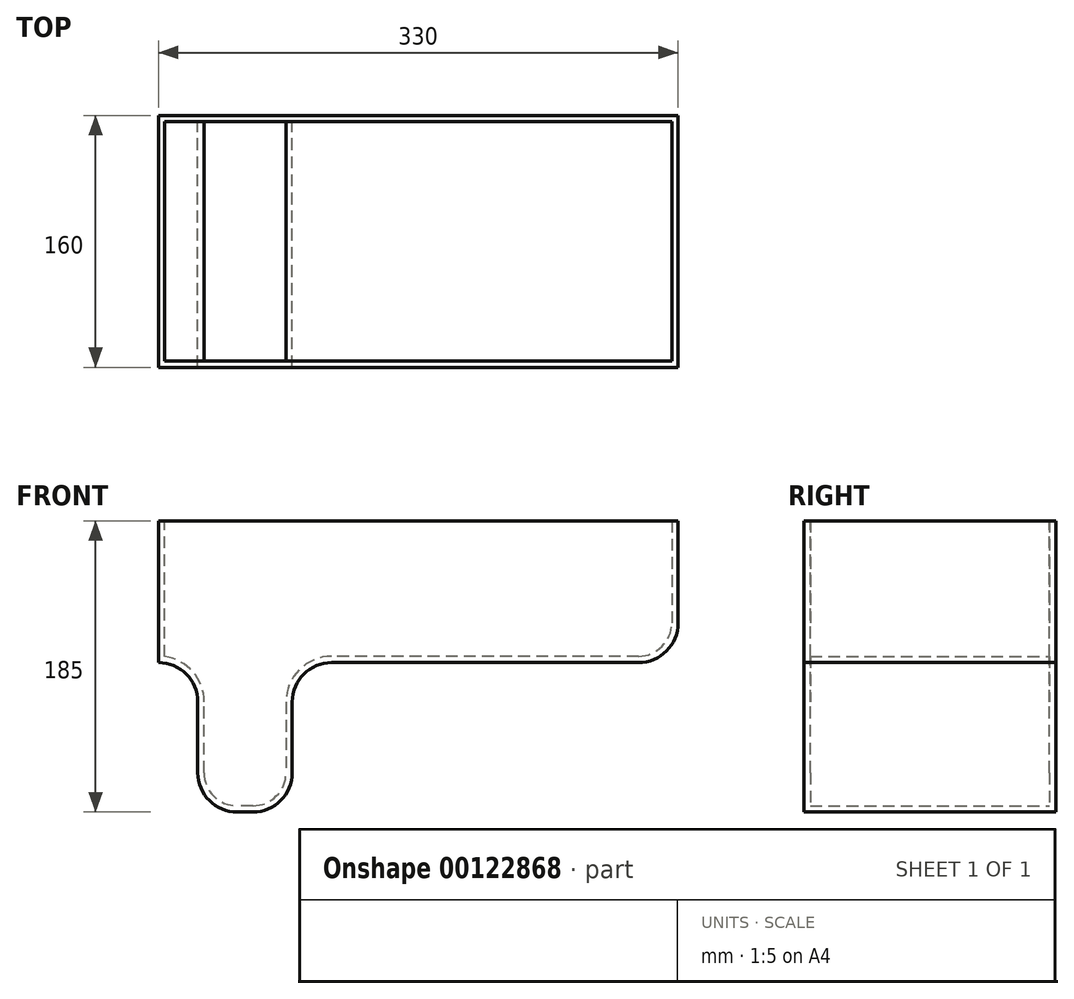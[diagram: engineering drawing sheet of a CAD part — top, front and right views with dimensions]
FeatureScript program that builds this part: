
annotation { "Feature Type Name" : "Feature", "Feature Type Description" : "" }
export const myFeature = defineFeature(function(context is Context, id is Id, definition is map)
    precondition{}
    {
        {
            var Q0;
            Q0=qCreatedBy(makeId("Front.planeOp"),FACE);
            var sketch = newSketch(context, id + "F0", { "sketchPlane" : qUnion([Q0])});
            skLineSegment(sketch, "E0", {"start": v(0, -25) * mm, "end": v(0, -70) * mm});
            skLineSegment(sketch, "E1", {"start": v(-25, -95) * mm, "end": v(-35, -95) * mm});
            skLineSegment(sketch, "E2", {"start": v(-60, -70) * mm, "end": v(-60, -25) * mm});
            skLineSegment(sketch, "E3", {"start": v(-85, 0) * mm, "end": v(-85, 0) * mm});
            skLineSegment(sketch, "E4", {"start": v(-85, 0) * mm, "end": v(-85, 90) * mm});
            skLineSegment(sketch, "E5", {"start": v(-85, 90) * mm, "end": v(245, 90) * mm});
            skLineSegment(sketch, "E6", {"start": v(245, 90) * mm, "end": v(245, 25) * mm});
            skLineSegment(sketch, "E7", {"start": v(220, 0) * mm, "end": v(25, 0) * mm});
            skPoint(sketch, "E8.visualSharp", {"position": v(245, 0) * mm});
            skArc(sketch, "E8.filletArc", {"start": v(220, 0) * mm, "mid": v(237.68, 7.32) * mm, "end": v(245, 25) * mm});
            skPoint(sketch, "E9.visualSharp", {"position": v(0, 0) * mm});
            skArc(sketch, "E9.filletArc", {"start": v(25, 0) * mm, "mid": v(7.32, -7.32) * mm, "end": v(0, -25) * mm});
            skPoint(sketch, "E10.visualSharp", {"position": v(0, -95) * mm});
            skArc(sketch, "E10.filletArc", {"start": v(-25, -95) * mm, "mid": v(-7.32, -87.68) * mm, "end": v(0, -70) * mm});
            skPoint(sketch, "E11.visualSharp", {"position": v(-60, -95) * mm});
            skArc(sketch, "E11.filletArc", {"start": v(-60, -70) * mm, "mid": v(-52.68, -87.68) * mm, "end": v(-35, -95) * mm});
            skPoint(sketch, "E12.visualSharp", {"position": v(-60, 0) * mm});
            skArc(sketch, "E12.filletArc", {"start": v(-60, -25) * mm, "mid": v(-67.32, -7.32) * mm, "end": v(-85, 0) * mm});
            skLineSegment(sketch, "E13", {"start": v(25, 0) * mm, "end": v(-85, 0) * mm});
            skSolve(sketch);
        }
        {
            var Q0;
            Q0=qSketchRegion(id+"F0",true);
            extrude(context, id + "F1", {"entities" : qUnion([Q0]), "depth" : 160 * mm});
        }
        {
            var Q0;
            Q0=qCreatedBy(makeId("Front.planeOp"),FACE);
            cPlane(context, id + "F2", {"entities" : qUnion([Q0]), "cplaneType" : CPlaneType.OFFSET, "offset" : 4 * mm, "width" : 150 * mm, "height" : 150 * mm});
        }
        {
            var Q0;
            Q0=qCreatedBy(id+"F2.planeOp",FACE);
            var sketch = newSketch(context, id + "F3", { "sketchPlane" : qUnion([Q0])});
            skArc(sketch, "E14.0", {"start": v(25, 0) * mm, "mid": v(7.32, -7.32) * mm, "end": v(0, -25) * mm});
            skLineSegment(sketch, "E15.0", {"start": v(0, -25) * mm, "end": v(0, -70) * mm});
            skArc(sketch, "E16.0", {"start": v(-25, -95) * mm, "mid": v(-7.32, -87.68) * mm, "end": v(0, -70) * mm});
            skLineSegment(sketch, "E17.0", {"start": v(-25, -95) * mm, "end": v(-35, -95) * mm});
            skArc(sketch, "E18.0", {"start": v(-60, -70) * mm, "mid": v(-52.68, -87.68) * mm, "end": v(-35, -95) * mm});
            skLineSegment(sketch, "E19.0", {"start": v(-60, -70) * mm, "end": v(-60, -25) * mm});
            skArc(sketch, "E20.0", {"start": v(-60, -25) * mm, "mid": v(-67.32, -7.32) * mm, "end": v(-85, 0) * mm});
            skLineSegment(sketch, "E21.6", {"start": v(-25, -91) * mm, "end": v(-35, -91) * mm});
            skLineSegment(sketch, "E22.1", {"start": v(-56, -70) * mm, "end": v(-56, -25) * mm});
            skArc(sketch, "E22.2", {"start": v(-56, -70) * mm, "mid": v(-49.85, -84.85) * mm, "end": v(-35, -91) * mm});
            skArc(sketch, "E22.3", {"start": v(25, 4) * mm, "mid": v(4.5, -4.5) * mm, "end": v(-4, -25) * mm});
            skLineSegment(sketch, "E22.4", {"start": v(-4, -25) * mm, "end": v(-4, -70) * mm});
            skArc(sketch, "E22.5", {"start": v(-25, -91) * mm, "mid": v(-10.15, -84.85) * mm, "end": v(-4, -70) * mm});
            skLineSegment(sketch, "E23.0", {"start": v(241, 90) * mm, "end": v(241, 25) * mm});
            skLineSegment(sketch, "E24.0", {"start": v(-81, 3.72) * mm, "end": v(-81, 90) * mm});
            skLineSegment(sketch, "E25.0", {"start": v(-85, 90) * mm, "end": v(245, 90) * mm});
            skLineSegment(sketch, "E26.0", {"start": v(220, 4) * mm, "end": v(25, 4) * mm});
            skArc(sketch, "E26.1", {"start": v(220, 4) * mm, "mid": v(234.85, 10.15) * mm, "end": v(241, 25) * mm});
            skArc(sketch, "E27.0", {"start": v(-56, -25) * mm, "mid": v(-63.13, -5.96) * mm, "end": v(-81, 3.72) * mm});
            skSolve(sketch);
        }
        {
            var Q0;
            Q0=qSketchRegion(id+"F3",true);
            extrude(context, id + "F4", {"entities" : qUnion([Q0]), "operationType" : NewBodyOperationType.REMOVE, "depth" : 152 * mm});
        }
    });
